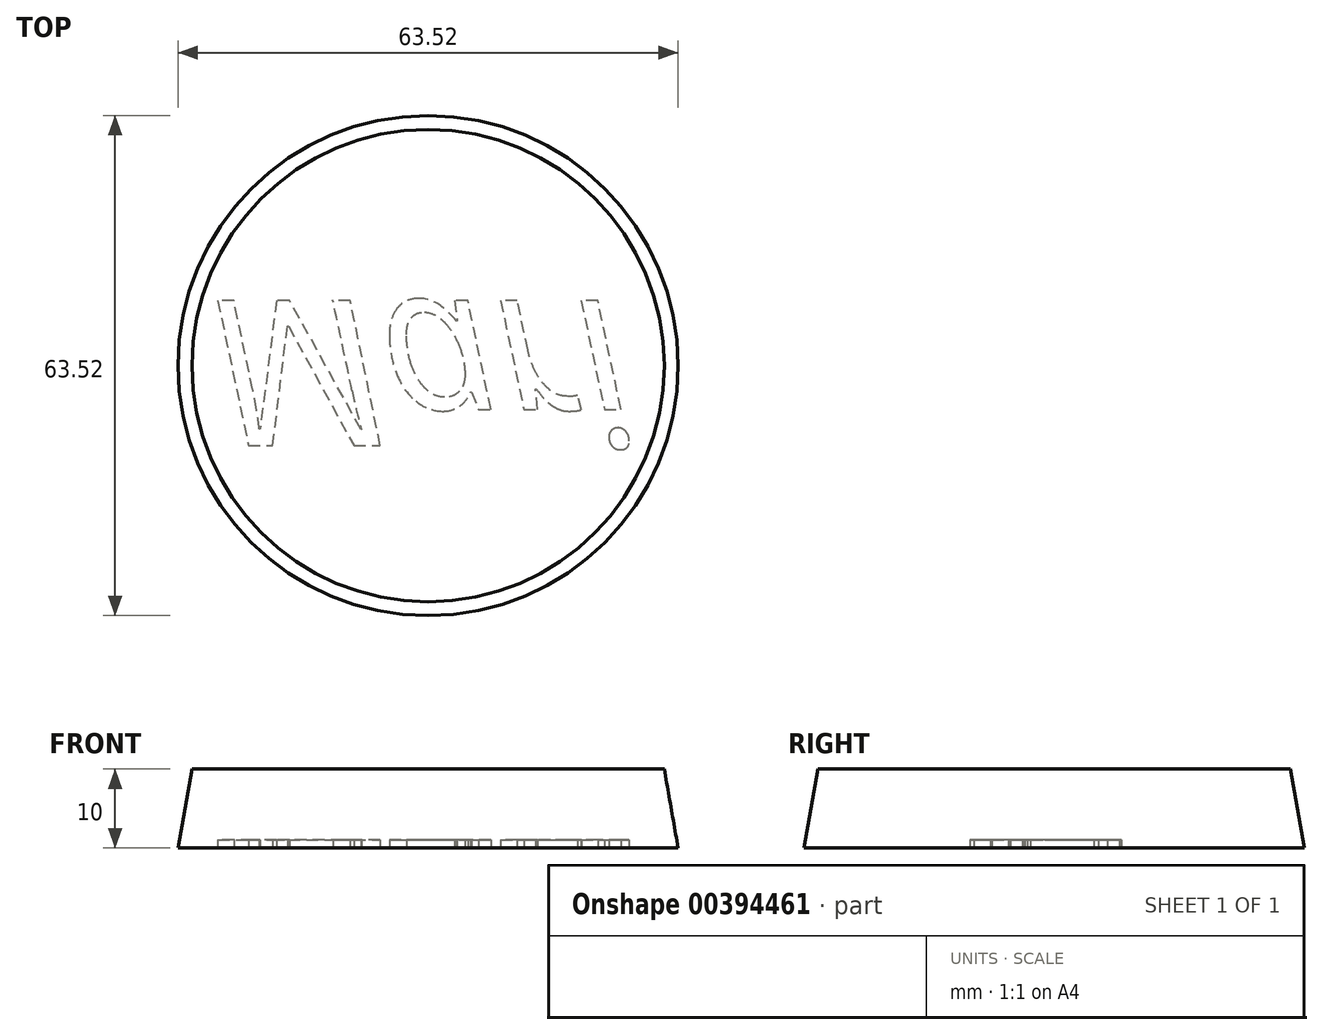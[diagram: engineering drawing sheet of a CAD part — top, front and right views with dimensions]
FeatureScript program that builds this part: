
annotation { "Feature Type Name" : "Feature", "Feature Type Description" : "" }
export const myFeature = defineFeature(function(context is Context, id is Id, definition is map)
    precondition{}
    {
        {
            var Q0;
            Q0=qCreatedBy(makeId("Top.planeOp"),FACE);
            var sketch = newSketch(context, id + "F0", { "sketchPlane" : qUnion([Q0])});
            skCircle(sketch, "E0", {"center": v(0, 0) * mm, "radius": 30 * mm});
            skSolve(sketch);
        }
        {
            var Q0;
            Q0=makeQuery(id+"F0.imprint","IMPRINT",FACE,{"disambiguationData":[TD([[makeQuery(id+"F0.imprint","IMPRINT",EDGE,{"derivedFrom":sQuery(id+"F0.wireOp",EDGE,"E0")}),1.0]])]});
            extrude(context, id + "F1", {"entities" : qUnion([Q0]), "oppositeDirection" : true, "depth" : 10 * mm, "hasDraft" : true, "draftAngle" : 10 * degree});
        }
        {
            var Q0;
            Q0=makeQuery(id+"F1.opExtrude","CAP_FACE",FACE,{"disambiguationData":[OSD([sQuery(id+"F0.wireOp",EDGE,"E0")])],"isStart":false});
            var sketch = newSketch(context, id + "F2", { "sketchPlane" : qUnion([Q0])});
            skText(sketch, "E1", { "text": "Mari", "fontName": "OpenSans-Italic.ttf"});
            const initialGuessF2  = {"E1": [-0.02778, -0.00829, 1, 0, 0.01861]};
            skSetInitialGuess(sketch, initialGuessF2);
            skSolve(sketch);
        }
        {
            var Q0;
            Q0=qSketchRegion(id+"F2",true);
            extrude(context, id + "F3", {"entities" : qUnion([Q0]), "operationType" : NewBodyOperationType.REMOVE, "oppositeDirection" : true, "depth" : 1 * mm});
        }
    });
